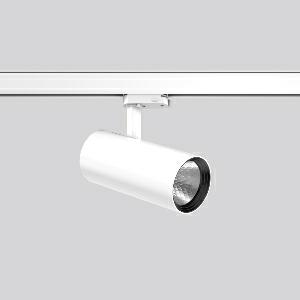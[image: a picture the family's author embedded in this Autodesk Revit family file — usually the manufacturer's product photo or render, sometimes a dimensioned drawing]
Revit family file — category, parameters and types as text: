
# Revit family: deecos_s_mini_742203_002_3_76_d7fd
name_source: partatom
category: Lighting Fixtures
units: mm (PartAtom-declared; Revit-internal decimal feet)

## family parameters
Cut with Voids When Loaded = No
Host = Face
Light Source = No
Part Type = Normal
Room Calculation Point = No
Round Connector Dimension = Use Diameter
Shared = No

## types (1)
- DEECOS S mini (1 x LED Modul 935, 3700 lm, 3500)
    Apparent Load = 29 VA
    Approval mark = CE
    CIE Flux Codes = 100 100 100 100 100
    Color Rendering = 92
    Color Temperature = 3500
    Default Elevation = 1800 mm
    Description = Series: DEECOS S mini
LED surface-mounted projector in modern design with no visible cooling ribs. Housing: die-cast aluminium, powder-coated. Rotation range: 356°. Swivel range: 90°. Black plastic ring and recessed LED to prevent glare from the side. Optical assembly with reflector made of MIRO-Silver with 98% total light reflection for outstanding efficiency - can be changed without tools. Best colour rendering index Ra>90. With adapter for RZB 3-circuit DALI tracks. Suitable for Track on ceiling, Wall track. High quality converter without flickering and stroboscopic effect. The following accessories can be mounted without use of tools: interchangeable lenses, decorative glasses, honeycomb louvre, clear and frosted diffusers, white interchangeable plastic ring. 
Colour: traffic white, matt (RAL 9016)
Diameter: 87 mm
Height: 214 mm
Lamp: LED
Socket: without socket
Colour temperature: 3500K
Colour rendering index (CRI): 92
System power: 29 W
Rated luminous flux: 3700 lm
Luminous efficiency: 128 lm/W
Control gear: Converter, dimmable, DALI
Protection class: I
Type of protection: IP 20
    Height = 214 mm
    Lamp = 1 x LED Modul 935
    Lamp Light Flux = 3700 lm
    Lamp count = 1
    Length = 87 mm
    Lifetime = 50000 h
    Luminous efficacy = 128 lm/W
    Manufacturer = RZB
    ModVariant = No
    Model = 742203.002.3.76
    Mounting Place = Ceiling
    Mounting Type = Rail mounted
    Number of Poles = 1
    OnlyDefault = Yes
    Power Factor = 1
    Product Name = DEECOS S mini
    Product group = Track mounted projectors
    ProductGroupID = 301
    Protection Class = Protection class I
    Protection Degree = IP 20
    RLX_Detail_Level = 1
    RLX_Emergency_Light_Flux = 0 lm
    RLX_Emergency_Type = 0
    RLX_Emergency_Type_DB = No
    RlxData = <blob elided: 35061 chars, md5=06adf247>
    Socket = socket
    Standby Power = 0 W
    System Light Flux = 3700 lm
    System Power = 29 W
    Type Comments = Product without accessories
    Type Image = 741926.002.jpg
    URL = http://relux.com
    VarID = ---
    Voltage = 230 V
    Voltage Range = 220-240 V
    Weight = 0.00 kg
    Width = 0 mm  [stored 0 ft]

note: [stored X ft] marks values corroborated as IEEE doubles in the binary element streams (Revit-internal decimal feet)

## geometry (parser evidence)
native form markers: Blend x4, Sweep x15
no freeform markers — native parametric forms only
